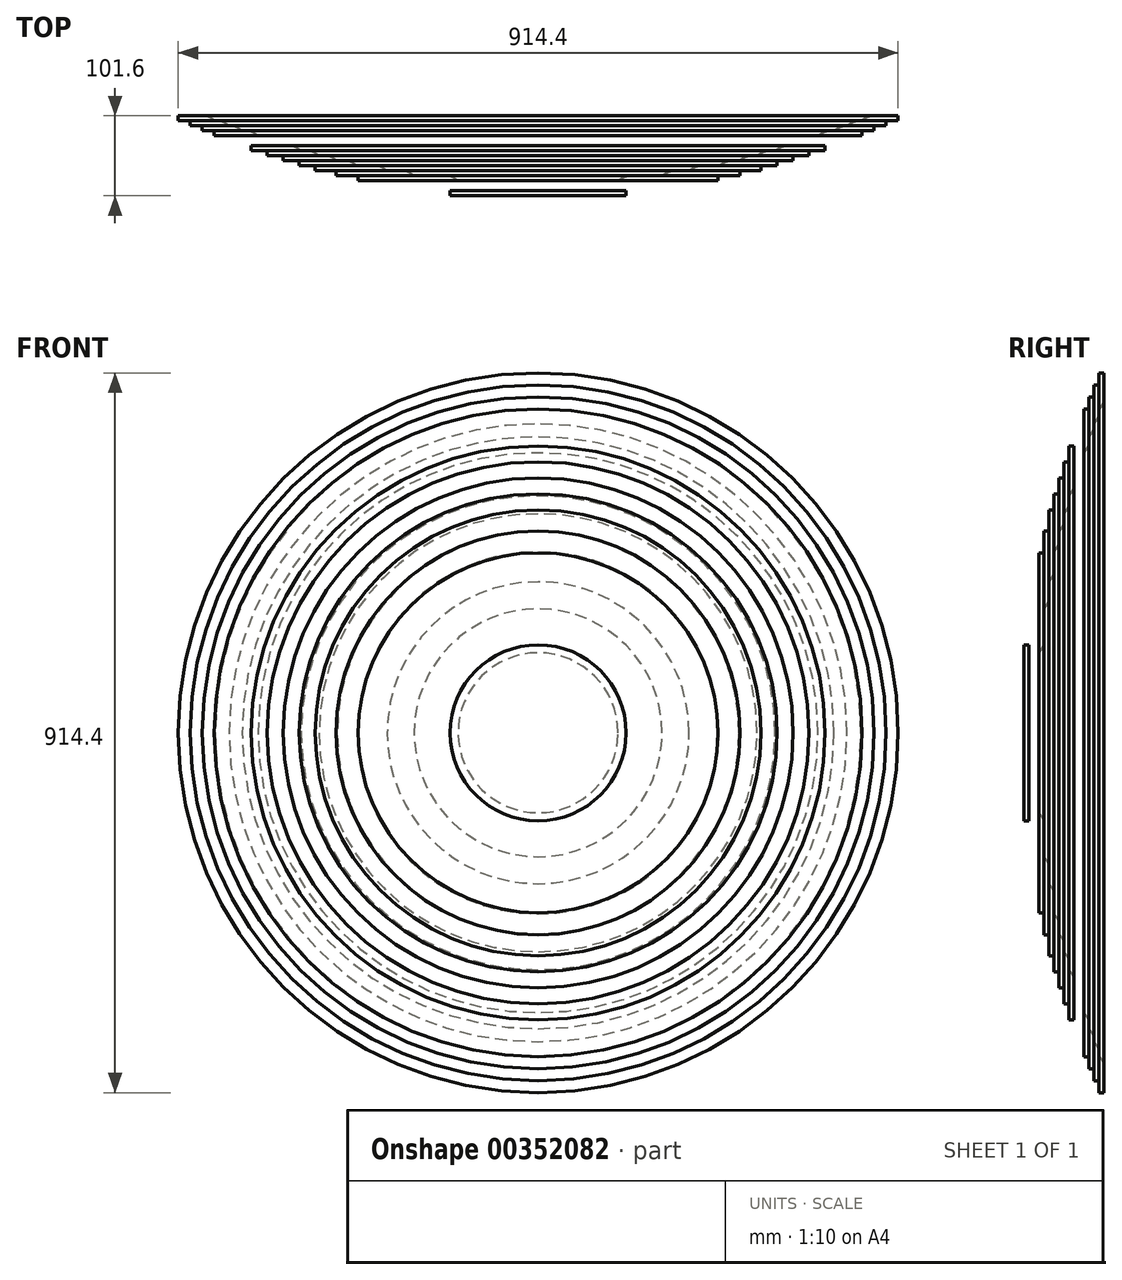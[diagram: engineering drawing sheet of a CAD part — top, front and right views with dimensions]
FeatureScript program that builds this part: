
annotation { "Feature Type Name" : "Feature", "Feature Type Description" : "" }
export const myFeature = defineFeature(function(context is Context, id is Id, definition is map)
    precondition{}
    {
        {
            var Q0;
            Q0=qCreatedBy(makeId("Top.planeOp"),FACE);
            var sketch = newSketch(context, id + "F0", { "sketchPlane" : qUnion([Q0])});
            skLineSegment(sketch, "E0", {"start": v(0, 0) * mm, "end": v(0, -101.6) * mm});
            skLineSegment(sketch, "E1", {"start": v(0, 0) * mm, "end": v(-457.2, 0) * mm});
            skLineSegment(sketch, "E2", {"start": v(0, 0) * mm, "end": v(457.2, 0) * mm});
            skArc(sketch, "E3", {"start": v(-457.2, 0) * mm, "mid": v(0, -101.6) * mm, "end": v(457.2, 0) * mm});
            skArc(sketch, "E4.0", {"start": v(-410.2, 0) * mm, "mid": v(0, -82.55) * mm, "end": v(410.2, 0) * mm});
            skSolve(sketch);
        }
        {
            var Q0;
            Q0=qCreatedBy(makeId("Front.planeOp"),FACE);
            var sketch = newSketch(context, id + "F1", { "sketchPlane" : qUnion([Q0])});
            skCircle(sketch, "E5", {"center": v(0, 0) * mm, "radius": 457.2 * mm});
            skCircle(sketch, "E6.0", {"center": v(0, 0) * mm, "radius": 410.21 * mm});
            skSolve(sketch);
        }
        {
            var Q0;
            Q0 = qSketchRegion(id + "F1", true);
            var Q1;
            Q1=makeQuery(id+"F1.imprint","IMPRINT",FACE,{"disambiguationData":[TD([[makeQuery(id+"F1.imprint","IMPRINT",EDGE,{"derivedFrom":sQuery(id+"F1.wireOp",EDGE,"dd74e99c-08bc-417e-bd63-acb364705c2e.0")}),1.0]])]});
            var Q2;
            Q2=makeQuery(id+"F1.imprint","IMPRINT",FACE,{"disambiguationData":[TD([[makeQuery(id+"F1.imprint","IMPRINT",EDGE,{"derivedFrom":sQuery(id+"F1.wireOp",EDGE,"d3dd813d-0c47-437d-9019-3aec181fee08.0")}),1.0]])]});
            extrude(context, id + "F2", {"entities" : qUnion([Q0, Q1, Q2]), "depth" : 6.35 * mm, "hasSecondDirection" : true, "secondDirectionOppositeDirection" : false, "secondDirectionDepth" : 0 * mm});
        }
        {
            var Q0;
            Q0=qCreatedBy(makeId("Front.planeOp"),FACE);
            var sketch = newSketch(context, id + "F3", { "sketchPlane" : qUnion([Q0])});
            skCircle(sketch, "E7", {"center": v(0, 0) * mm, "radius": 441.96 * mm});
            skCircle(sketch, "E8.0", {"center": v(0, 0) * mm, "radius": 392.43 * mm});
            skSolve(sketch);
        }
        {
            var Q0;
            Q0 = qSketchRegion(id + "F3", true);
            extrude(context, id + "F4", {"entities" : qUnion([Q0]), "operationType" : NewBodyOperationType.ADD, "depth" : 12.7 * mm, "hasSecondDirection" : true, "secondDirectionOppositeDirection" : false, "secondDirectionDepth" : 6.35 * mm});
        }
        {
            var Q0;
            Q0=qCreatedBy(makeId("Front.planeOp"),FACE);
            var sketch = newSketch(context, id + "F5", { "sketchPlane" : qUnion([Q0])});
            skCircle(sketch, "E9", {"center": v(0, 0) * mm, "radius": 426.72 * mm});
            skCircle(sketch, "E10.0", {"center": v(0, 0) * mm, "radius": 375.92 * mm});
            skSolve(sketch);
        }
        {
            var Q0;
            Q0 = qSketchRegion(id + "F5", true);
            extrude(context, id + "F6", {"entities" : qUnion([Q0]), "depth" : 19.05 * mm, "hasSecondDirection" : true, "secondDirectionOppositeDirection" : false, "secondDirectionDepth" : 12.7 * mm});
        }
        {
            var Q0;
            Q0=qCreatedBy(makeId("Front.planeOp"),FACE);
            var sketch = newSketch(context, id + "F7", { "sketchPlane" : qUnion([Q0])});
            skCircle(sketch, "E11", {"center": v(0, 0) * mm, "radius": 411.48 * mm});
            skCircle(sketch, "E12.0", {"center": v(0, 0) * mm, "radius": 355.6 * mm});
            skSolve(sketch);
        }
        {
            var Q0;
            Q0 = qSketchRegion(id + "F7", true);
            extrude(context, id + "F8", {"entities" : qUnion([Q0]), "depth" : 25.4 * mm, "hasSecondDirection" : true, "secondDirectionOppositeDirection" : false, "secondDirectionDepth" : 19.05 * mm});
        }
        {
            var Q0;
            Q0=qCreatedBy(makeId("Front.planeOp"),FACE);
            var sketch = newSketch(context, id + "F9", { "sketchPlane" : qUnion([Q0])});
            skCircle(sketch, "E13", {"center": v(0, 0) * mm, "radius": 396.24 * mm});
            skCircle(sketch, "E14.0", {"center": v(0, 0) * mm, "radius": 340.36 * mm});
            skSolve(sketch);
        }
        {
            var Q0;
            Q0=qCreatedBy(makeId("Front.planeOp"),FACE);
            var sketch = newSketch(context, id + "F10", { "sketchPlane" : qUnion([Q0])});
            skCircle(sketch, "E15", {"center": v(0, 0) * mm, "radius": 381 * mm});
            skCircle(sketch, "E16.0", {"center": v(0, 0) * mm, "radius": 322.58 * mm});
            skSolve(sketch);
        }
        {
            var Q0;
            Q0=qCreatedBy(makeId("Front.planeOp"),FACE);
            var sketch = newSketch(context, id + "F11", { "sketchPlane" : qUnion([Q0])});
            skCircle(sketch, "E17", {"center": v(0, 0) * mm, "radius": 364.5 * mm});
            skCircle(sketch, "E18.0", {"center": v(0, 0) * mm, "radius": 301 * mm});
            skSolve(sketch);
        }
        {
            var Q0;
            Q0 = qSketchRegion(id + "F11", true);
            extrude(context, id + "F12", {"entities" : qUnion([Q0]), "operationType" : NewBodyOperationType.ADD, "depth" : 44.45 * mm, "hasSecondDirection" : true, "secondDirectionOppositeDirection" : false, "secondDirectionDepth" : 38.1 * mm});
        }
        {
            var Q0;
            Q0=qCreatedBy(makeId("Front.planeOp"),FACE);
            var sketch = newSketch(context, id + "F13", { "sketchPlane" : qUnion([Q0])});
            skCircle(sketch, "E19", {"center": v(0, 0) * mm, "radius": 344.17 * mm});
            skCircle(sketch, "E20.0", {"center": v(0, 0) * mm, "radius": 278.13 * mm});
            skSolve(sketch);
        }
        {
            var Q0;
            Q0 = qSketchRegion(id + "F13", true);
            extrude(context, id + "F14", {"entities" : qUnion([Q0]), "operationType" : NewBodyOperationType.ADD, "depth" : 50.8 * mm, "hasSecondDirection" : true, "secondDirectionOppositeDirection" : false, "secondDirectionDepth" : 44.45 * mm});
        }
        {
            var Q0;
            Q0=qCreatedBy(makeId("Front.planeOp"),FACE);
            var sketch = newSketch(context, id + "F15", { "sketchPlane" : qUnion([Q0])});
            skCircle(sketch, "E21", {"center": v(0, 0) * mm, "radius": 323.85 * mm});
            skCircle(sketch, "E22.0", {"center": v(0, 0) * mm, "radius": 255.27 * mm});
            skSolve(sketch);
        }
        {
            var Q0;
            Q0 = qSketchRegion(id + "F15", true);
            extrude(context, id + "F16", {"entities" : qUnion([Q0]), "operationType" : NewBodyOperationType.ADD, "depth" : 57.15 * mm, "hasSecondDirection" : true, "secondDirectionOppositeDirection" : false, "secondDirectionDepth" : 50.8 * mm});
        }
        {
            var Q0;
            Q0=qCreatedBy(makeId("Front.planeOp"),FACE);
            var sketch = newSketch(context, id + "F17", { "sketchPlane" : qUnion([Q0])});
            skCircle(sketch, "E23", {"center": v(0, 0) * mm, "radius": 303.53 * mm});
            skCircle(sketch, "E24.0", {"center": v(0, 0) * mm, "radius": 229.87 * mm});
            skSolve(sketch);
        }
        {
            var Q0;
            Q0 = qSketchRegion(id + "F17", true);
            extrude(context, id + "F18", {"entities" : qUnion([Q0]), "operationType" : NewBodyOperationType.ADD, "depth" : 63.5 * mm, "hasSecondDirection" : true, "secondDirectionOppositeDirection" : false, "secondDirectionDepth" : 57.15 * mm});
        }
        {
            var Q0;
            Q0=qCreatedBy(makeId("Front.planeOp"),FACE);
            var sketch = newSketch(context, id + "F19", { "sketchPlane" : qUnion([Q0])});
            skCircle(sketch, "E25", {"center": v(0, 0) * mm, "radius": 283.21 * mm});
            skCircle(sketch, "E26.0", {"center": v(0, 0) * mm, "radius": 191.77 * mm});
            skSolve(sketch);
        }
        {
            var Q0;
            Q0 = qSketchRegion(id + "F19", true);
            extrude(context, id + "F20", {"entities" : qUnion([Q0]), "operationType" : NewBodyOperationType.ADD, "depth" : 69.85 * mm, "hasSecondDirection" : true, "secondDirectionOppositeDirection" : false, "secondDirectionDepth" : 63.5 * mm});
        }
        {
            var Q0;
            Q0=qCreatedBy(makeId("Front.planeOp"),FACE);
            var sketch = newSketch(context, id + "F21", { "sketchPlane" : qUnion([Q0])});
            skCircle(sketch, "E27", {"center": v(0, 0) * mm, "radius": 256.54 * mm});
            skCircle(sketch, "E28.0", {"center": v(0, 0) * mm, "radius": 157.48 * mm});
            skSolve(sketch);
        }
        {
            var Q0;
            Q0 = qSketchRegion(id + "F21", true);
            extrude(context, id + "F22", {"entities" : qUnion([Q0]), "operationType" : NewBodyOperationType.ADD, "depth" : 76.2 * mm, "hasSecondDirection" : true, "secondDirectionOppositeDirection" : false, "secondDirectionDepth" : 69.85 * mm});
        }
        {
            var Q0;
            Q0=qCreatedBy(makeId("Front.planeOp"),FACE);
            var sketch = newSketch(context, id + "F23", { "sketchPlane" : qUnion([Q0])});
            skCircle(sketch, "E29", {"center": v(0, 0) * mm, "radius": 228.6 * mm});
            skCircle(sketch, "E30.0", {"center": v(0, 0) * mm, "radius": 101.6 * mm});
            skSolve(sketch);
        }
        {
            var Q0;
            Q0 = qSketchRegion(id + "F23", true);
            extrude(context, id + "F24", {"entities" : qUnion([Q0]), "operationType" : NewBodyOperationType.ADD, "depth" : 82.55 * mm, "hasSecondDirection" : true, "secondDirectionOppositeDirection" : false, "secondDirectionDepth" : 76.2 * mm});
        }
        {
            var Q0;
            Q0=qCreatedBy(makeId("Front.planeOp"),FACE);
            var sketch = newSketch(context, id + "F25", { "sketchPlane" : qUnion([Q0])});
            skCircle(sketch, "E31", {"center": v(0, 0) * mm, "radius": 199.4 * mm});
            skSolve(sketch);
        }
        {
            var Q0;
            Q0=makeQuery(id+"F2.opExtrude","CAP_EDGE",EDGE,{"disambiguationData":[OSD([sQuery(id+"F1.wireOp",EDGE,"E6.0")])],"isStart":true});
            var Q1;
            Q1=makeQuery(id+"F4.opExtrude","CAP_EDGE",EDGE,{"disambiguationData":[OSD([sQuery(id+"F3.wireOp",EDGE,"E8.0")])],"isStart":true});
            var Q2;
            Q2=makeQuery(id+"F6.opExtrude","CAP_EDGE",EDGE,{"disambiguationData":[OSD([sQuery(id+"F5.wireOp",EDGE,"E10.0")])],"isStart":true});
            var Q3;
            Q3=makeQuery(id+"F8.opExtrude","CAP_EDGE",EDGE,{"disambiguationData":[OSD([sQuery(id+"F7.wireOp",EDGE,"E12.0")])],"isStart":true});
            var Q4;
            Q4=makeQuery(id+"FUBoNAKGu8mOtz2_2.opExtrude","CAP_EDGE",EDGE,{"disambiguationData":[OSD([sQuery(id+"F9.wireOp",EDGE,"E14.0")])],"isStart":true});
            var Q5;
            Q5=makeQuery(id+"F93LNEBcappiM3o_3.opExtrude","CAP_EDGE",EDGE,{"disambiguationData":[OSD([sQuery(id+"F10.wireOp",EDGE,"E16.0")])],"isStart":true});
            var Q6;
            Q6=makeQuery(id+"F12.opExtrude","CAP_EDGE",EDGE,{"disambiguationData":[OSD([sQuery(id+"F11.wireOp",EDGE,"E18.0")])],"isStart":true});
            var Q7;
            Q7=makeQuery(id+"F14.opExtrude","CAP_EDGE",EDGE,{"disambiguationData":[OSD([sQuery(id+"F13.wireOp",EDGE,"E20.0")])],"isStart":true});
            var Q8;
            Q8=makeQuery(id+"F16.opExtrude","CAP_EDGE",EDGE,{"disambiguationData":[OSD([sQuery(id+"F15.wireOp",EDGE,"E22.0")])],"isStart":true});
            var Q9;
            Q9=makeQuery(id+"F18.opExtrude","CAP_EDGE",EDGE,{"disambiguationData":[OSD([sQuery(id+"F17.wireOp",EDGE,"E24.0")])],"isStart":true});
            var Q10;
            Q10=makeQuery(id+"F20.opExtrude","CAP_EDGE",EDGE,{"disambiguationData":[OSD([sQuery(id+"F19.wireOp",EDGE,"E26.0")])],"isStart":true});
            var Q11;
            Q11=makeQuery(id+"F22.opExtrude","CAP_EDGE",EDGE,{"disambiguationData":[OSD([sQuery(id+"F21.wireOp",EDGE,"E28.0")])],"isStart":true});
            var Q12;
            Q12=makeQuery(id+"F24.opExtrude","CAP_EDGE",EDGE,{"disambiguationData":[OSD([sQuery(id+"F23.wireOp",EDGE,"E30.0")])],"isStart":true});
            fillet(context, id + "F26", {"entities" : qUnion([Q0, Q1, Q2, Q3, Q4, Q5, Q6, Q7, Q8, Q9, Q10, Q11, Q12]), "radius" : 25.4 * mm, "tangentPropagation" : true, "allowEdgeOverflow" : false});
        }
        {
            var Q0;
            Q0=qCreatedBy(makeId("Front.planeOp"),FACE);
            var sketch = newSketch(context, id + "F27", { "sketchPlane" : qUnion([Q0])});
            skCircle(sketch, "E32", {"center": v(0, 0) * mm, "radius": 160.02 * mm});
            skSolve(sketch);
        }
        {
            var Q0;
            Q0=qCreatedBy(makeId("Front.planeOp"),FACE);
            var sketch = newSketch(context, id + "F28", { "sketchPlane" : qUnion([Q0])});
            skCircle(sketch, "E33", {"center": v(0, 0) * mm, "radius": 111.76 * mm});
            skSolve(sketch);
        }
        {
            var Q0;
            Q0 = qSketchRegion(id + "F28", true);
            extrude(context, id + "F29", {"entities" : qUnion([Q0]), "operationType" : NewBodyOperationType.ADD, "depth" : 101.6 * mm, "hasSecondDirection" : true, "secondDirectionOppositeDirection" : false, "secondDirectionDepth" : 95.25 * mm});
        }
    });
